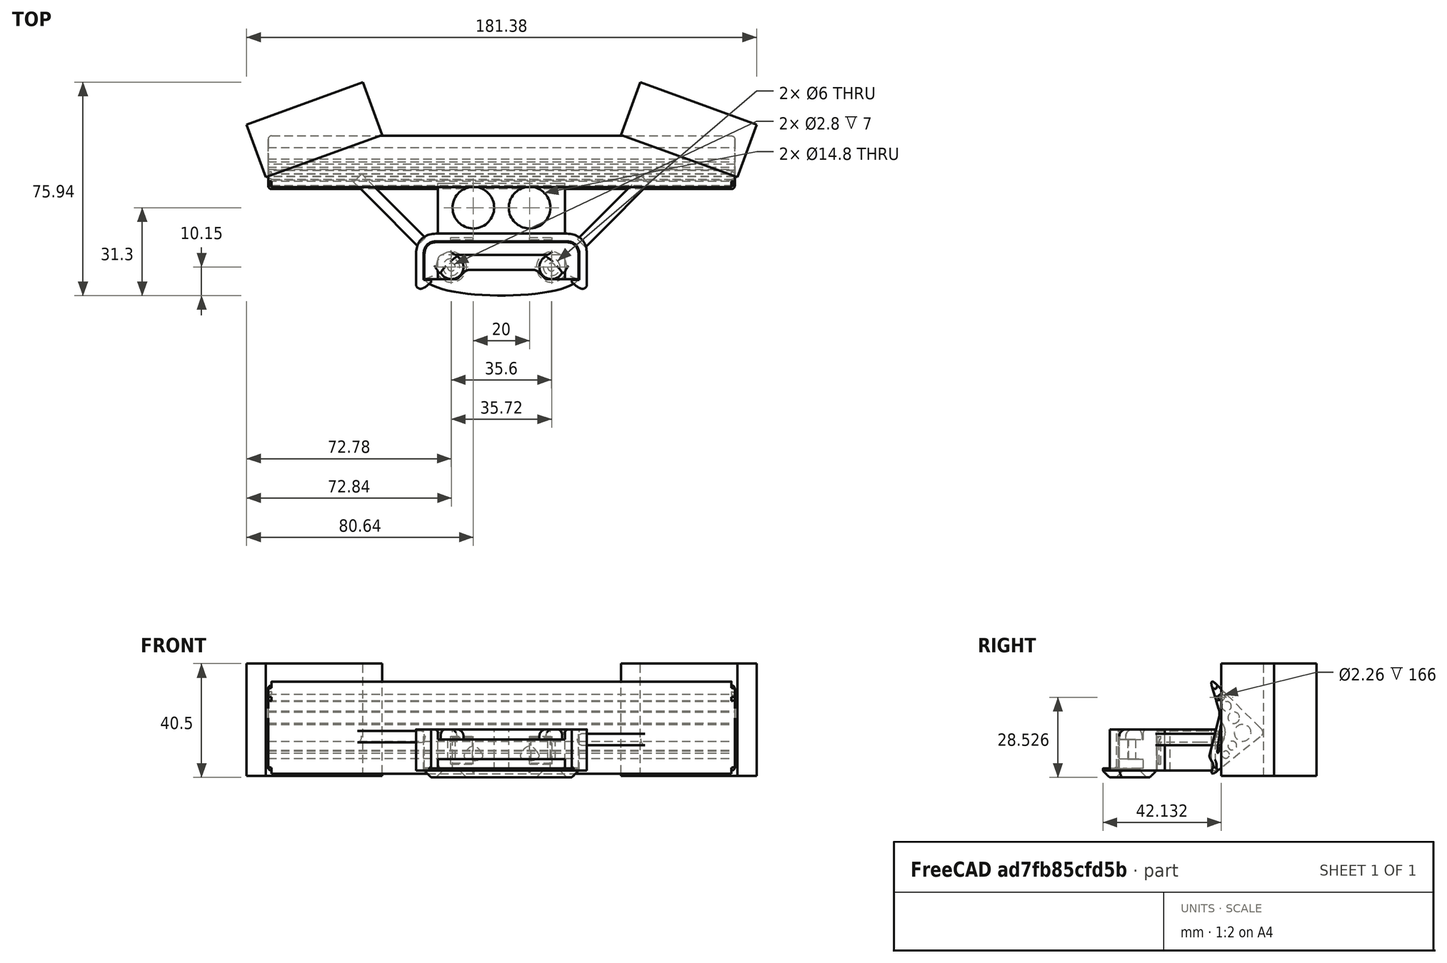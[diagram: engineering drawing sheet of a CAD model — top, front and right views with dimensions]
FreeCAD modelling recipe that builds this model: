
FCSTD DOCUMENT  (FreeCAD 0.21R0.20.1)
Label: 052
License: All rights reserved
LicenseURL: http://en.wikipedia.org/wiki/All_rights_reserved
objects: Part::Cylinder×8, Sketcher::SketchObject×7, Part::Extrusion×7, Part::Box×7, Part::MultiFuse×7, Part::Fillet×7, Part::Cut×4, Part::Chamfer×2
note: 49 computed .brp shape members not serialized (recipe doc carries the construction recipe); baked Part::Feature solids carry a one-line shape summary decoded from their .brp

FEATURE [Sketcher::SketchObject] Sketch  label="attatchmentPiece"
  FullyConstrained = true
  sketch-geometry (20):
    g0: LineSegment StartX=21.05 StartY=0 StartZ=0 EndX=21.05 EndY=-1 EndZ=0
    g1: LineSegment StartX=21.05 StartY=-1 StartZ=0 EndX=21.05 EndY=-4.3 EndZ=0
    g2: LineSegment StartX=-24.15 StartY=4.3 StartZ=0 EndX=21.05 EndY=4.3 EndZ=0
    g3: LineSegment StartX=21.05 StartY=0 StartZ=0 EndX=21.05 EndY=4.3 EndZ=0
    g4-g7: Circle x4 (B-spline internal-alignment scaffolding for g8; pole/knot coordinates omitted)
    g8: BSplineCurve PolesCount=4 KnotsCount=2 Degree=3 IsPeriodic=0
    g9: GeomPoint X=10.05 Y=-1 Z=0
    g10: GeomPoint X=14.55 Y=-4.3 Z=0
    g11: LineSegment StartX=10.05 StartY=-1 StartZ=0 EndX=-10.05 EndY=-1 EndZ=0
    g12: LineSegment StartX=14.55 StartY=-4.3 StartZ=0 EndX=21.05 EndY=-4.3 EndZ=0
    g13: LineSegment StartX=-24.15 StartY=4.3 StartZ=0 EndX=-24.15 EndY=-4.3 EndZ=0
    g14: LineSegment StartX=-13.15 StartY=-1 StartZ=0 EndX=-10.05 EndY=-1 EndZ=0
    g15: LineSegment StartX=-24.15 StartY=-4.3 StartZ=0 EndX=-19.35 EndY=-4.3 EndZ=0
    g16: LineSegment StartX=-19.35 StartY=-4.3 StartZ=0 EndX=-17.65 EndY=-4.3 EndZ=0
    g17: BSplineCurve PolesCount=4 KnotsCount=2 Degree=3 IsPeriodic=0
    g18: Circle CenterX=16.25 CenterY=0 CenterZ=0 NormalX=0 NormalY=0 NormalZ=1 AngleXU=0 Radius=1.4
    g19: Circle CenterX=-19.35 CenterY=0 CenterZ=0 NormalX=0 NormalY=0 NormalZ=1 AngleXU=0 Radius=1.4
  constraints (41):
    c: Vertical(g0)
    c: Coincident(g1,g0)
    c: Vertical(g1)
    c: Block(g0)
    c: Horizontal(g2)
    c: Vertical(g3)
    c: Coincident(g3,g2)
    c: Block(g2)
    c: Block(g3)
    c: Weight(g4) = 1
    c: Equal(g4,g5)
    c: Equal(g4,g6)
    c: Equal(g4,g7)
    c: InternalAlignment(g4-g7 -> g8) x4
    c: InternalAlignment(g9,g8)
    c: InternalAlignment(g10,g8)
    c: Block(g8)
    c: Coincident(g11,g8)
    c: Horizontal(g11)
    c: Coincident(g12,g8)
    c: Coincident(g12,g1)
    c: Horizontal(g12)
    c: Distance(g2) = 45.2
    c: Coincident(g13,g2)
    c: Vertical(g13)
    c: Horizontal(g14)
    c: Distance(g14) = 3.1
    c: Horizontal(g15)
    c: Block(g17)
    c: Coincident(g16,g15)
    c: Coincident(g16,g17)
    c: Horizontal(g16)
    c: Block(g16)
    c: Coincident(g17,g14)
    c: Block(g15)
    c: Block(g11)
    c: Block(g13)
    c: Distance(g15) = 4.8
    c: Distance(g16) = 1.7
    c: Block(g18)
    c: Block(g19)
FEATURE [Part::Extrusion] Extrude  label="attatchmentPiece001"
  Base = -> Sketch
  Dir = (0,0,1)
  DirMode = 2
  FaceMakerClass = Part::FaceMakerBullseye
  LengthFwd = 7
  LengthRev = 0
  Solid = true
  Symmetric = false
FEATURE [Sketcher::SketchObject] Sketch001  label="attatchmentPieceSurround"
  FullyConstrained = true
  sketch-geometry (18):
    g0: LineSegment StartX=25.85 StartY=-4.3 StartZ=0 EndX=21.05 EndY=-4.3 EndZ=0
    g1: LineSegment StartX=25.85 StartY=-4.3 StartZ=0 EndX=25.85 EndY=4.3 EndZ=0
    g2: LineSegment StartX=-21.05 StartY=8.9 StartZ=0 EndX=21.05 EndY=8.9 EndZ=0
    g3: Circle CenterX=21.05 CenterY=8.9 CenterZ=0 NormalX=0 NormalY=0 NormalZ=1 AngleXU=0 Radius=1
    g4: Circle CenterX=25.85 CenterY=8.9 CenterZ=0 NormalX=0 NormalY=0 NormalZ=1 AngleXU=0 Radius=1
    g5: Circle CenterX=25.85 CenterY=4.3 CenterZ=0 NormalX=0 NormalY=0 NormalZ=1 AngleXU=0 Radius=1
    g6: BSplineCurve PolesCount=3 KnotsCount=2 Degree=2 IsPeriodic=0
    g7: GeomPoint X=21.05 Y=8.9 Z=0
    g8: GeomPoint X=25.85 Y=4.3 Z=0
    g9: ArcOfCircle CenterX=19.45 CenterY=2.7 CenterZ=0 NormalX=0 NormalY=0 NormalZ=1 AngleXU=0 Radius=1.6 StartAngle=0 EndAngle=1.5708
    g10: LineSegment StartX=21.05 StartY=2.7 StartZ=0 EndX=21.05 EndY=-4.3 EndZ=0
    g11: BSplineCurve PolesCount=3 KnotsCount=2 Degree=2 IsPeriodic=0
    g12: LineSegment StartX=-28.95 StartY=-4.3 StartZ=0 EndX=-28.95 EndY=4.3 EndZ=0
    g13: LineSegment StartX=-24.15 StartY=-4.3 StartZ=0 EndX=-28.95 EndY=-4.3 EndZ=0
    g14: LineSegment StartX=-24.15 StartY=2.7 StartZ=0 EndX=-24.15 EndY=-4.3 EndZ=0
    g15: ArcOfCircle CenterX=-22.55 CenterY=2.7 CenterZ=0 NormalX=0 NormalY=0 NormalZ=1 AngleXU=0 Radius=1.6 StartAngle=1.5708 EndAngle=3.14159
    g16: LineSegment StartX=-24.15 StartY=8.9 StartZ=0 EndX=-21.05 EndY=8.9 EndZ=0
    g17: LineSegment StartX=-22.55 StartY=4.3 StartZ=0 EndX=19.45 EndY=4.3 EndZ=0
  constraints (38):
    c: Horizontal(g0)
    c: Vertical(g1)
    c: Coincident(g1,g0)
    c: Horizontal(g2)
    c: Distance(g2) = 42.1
    c: Block(g2)
    c: Coincident(g6,g2)
    c: Weight(g3) = 1
    c: Equal(g3,g4)
    c: Equal(g3,g5)
    c: Coincident(g6,g1)
    c: InternalAlignment(g3,g6)
    c: InternalAlignment(g4,g6)
    c: InternalAlignment(g5,g6)
    c: InternalAlignment(g7,g6)
    c: InternalAlignment(g8,g6)
    c: Block(g0)
    c: Block(g6)
    c: Block(g9)
    c: Coincident(g10,g9)
    c: Coincident(g10,g0)
    c: Vertical(g10)
    c: Horizontal(g13)
    c: Coincident(g12,g13)
    c: Vertical(g12)
    c: Coincident(g11,g12)
    c: Block(g12)
    c: Block(g11)
    c: Block(g15)
    c: Coincident(g14,g15)
    c: Coincident(g14,g13)
    c: Vertical(g14)
    c: Coincident(g16,g11)
    c: Coincident(g16,g2)
    c: Horizontal(g16)
    c: Coincident(g17,g15)
    c: Coincident(g17,g9)
    c: Horizontal(g17)
FEATURE [Part::Extrusion] Extrude001  label="attatchmentPieceSurround001"
  Base = -> Sketch001
  Dir = (0,0,1)
  DirMode = 2
  FaceMakerClass = Part::FaceMakerBullseye
  LengthFwd = 14.7
  LengthRev = 0
  Placement = pos=(0,0,-4.1) rot=(0,0,1;0rad)
  Solid = true
  Symmetric = false
FEATURE [Sketcher::SketchObject] Sketch002  label="attatchmentPieceEndScrewHoleCaps"
  FullyConstrained = true
  sketch-geometry (10):
    g0: ArcOfCircle CenterX=16.25 CenterY=0 CenterZ=0 NormalX=0 NormalY=0 NormalZ=1 AngleXU=0 Radius=4.3 StartAngle=2.05456 EndAngle=5.79942
    g1: LineSegment StartX=14.25 StartY=3.80657 StartZ=0 EndX=14.25 EndY=6 EndZ=0
    g2: LineSegment StartX=20.0566 StartY=-2 StartZ=0 EndX=22.25 EndY=-2 EndZ=0
    g3: LineSegment StartX=22.25 StartY=-2 StartZ=0 EndX=22.25 EndY=6 EndZ=0
    g4: LineSegment StartX=14.25 StartY=6 StartZ=0 EndX=22.25 EndY=6 EndZ=0
    g5: LineSegment StartX=-25.35 StartY=-2 StartZ=0 EndX=-25.35 EndY=6 EndZ=0
    g6: LineSegment StartX=-25.35 StartY=-2 StartZ=0 EndX=-23.1566 EndY=-2 EndZ=0
    g7: LineSegment StartX=-17.35 StartY=6 StartZ=0 EndX=-25.35 EndY=6 EndZ=0
    g8: LineSegment StartX=-17.35 StartY=3.80657 StartZ=0 EndX=-17.35 EndY=6 EndZ=0
    g9: ArcOfCircle CenterX=-19.35 CenterY=0 CenterZ=0 NormalX=0 NormalY=0 NormalZ=1 AngleXU=0 Radius=4.3 StartAngle=3.62536 EndAngle=7.37022
  constraints (25):
    c: Block(g0)
    c: Vertical(g1)
    c: Horizontal(g2)
    c: Coincident(g3,g2)
    c: Vertical(g3)
    c: Coincident(g4,g1)
    c: Horizontal(g4)
    c: Coincident(g3,g4)
    c: Block(g4)
    c: Block(g3)
    c: Coincident(g0,g1)
    c: Coincident(g0,g2)
    c: Block(g1)
    c: Block(g9)
    c: Horizontal(g6)
    c: Vertical(g8)
    c: Coincident(g7,g8)
    c: Horizontal(g7)
    c: Coincident(g5,g6)
    c: Vertical(g5)
    c: Coincident(g5,g7)
    c: Block(g7)
    c: Block(g5)
    c: Coincident(g9,g6)
    c: Coincident(g9,g8)
FEATURE [Part::Extrusion] Extrude002  label="attatchmentPieceEndScrewHoleCaps001"
  Base = -> Sketch002
  Dir = (0,0,1)
  DirMode = 2
  FaceMakerClass = Part::FaceMakerBullseye
  LengthFwd = 3.6
  LengthRev = 0
  Placement = pos=(0,0,7) rot=(0,0,1;0rad)
  Solid = true
  Symmetric = false
FEATURE [Sketcher::SketchObject] Sketch003  label="mainBumpperPieceAttatchment"
  FullyConstrained = true
  sketch-geometry (42):
    g0: Circle CenterX=28.85 CenterY=4.3 CenterZ=0 NormalX=0 NormalY=0 NormalZ=1 AngleXU=0 Radius=1
    g1: Circle CenterX=28.85 CenterY=11.9 CenterZ=0 NormalX=0 NormalY=0 NormalZ=1 AngleXU=0 Radius=1
    g2: Circle CenterX=21.05 CenterY=11.9 CenterZ=0 NormalX=0 NormalY=0 NormalZ=1 AngleXU=0 Radius=1
    g3: BSplineCurve PolesCount=3 KnotsCount=2 Degree=2 IsPeriodic=0
    g4: GeomPoint X=28.85 Y=4.3 Z=0
    g5: GeomPoint X=21.05 Y=11.9 Z=0
    g6: LineSegment StartX=-21.05 StartY=11.9 StartZ=0 EndX=21.05 EndY=11.9 EndZ=0
    g7: LineSegment StartX=28.85 StartY=4.3 StartZ=0 EndX=28.85 EndY=-4.3 EndZ=0
    g8: Circle CenterX=21.05 CenterY=9.2 CenterZ=0 NormalX=0 NormalY=0 NormalZ=1 AngleXU=0 Radius=1
    g9: Circle CenterX=26.15 CenterY=9.2 CenterZ=0 NormalX=0 NormalY=0 NormalZ=1 AngleXU=0 Radius=1
    g10: Circle CenterX=26.15 CenterY=4.3 CenterZ=0 NormalX=0 NormalY=0 NormalZ=1 AngleXU=0 Radius=1
    g11: BSplineCurve PolesCount=3 KnotsCount=2 Degree=2 IsPeriodic=0
    g12: GeomPoint X=21.05 Y=9.2 Z=0
    g13: GeomPoint X=26.15 Y=4.3 Z=0
    g14: LineSegment StartX=-21.05 StartY=9.2 StartZ=0 EndX=21.05 EndY=9.2 EndZ=0
    g15: LineSegment StartX=26.15 StartY=-4.3 StartZ=0 EndX=26.15 EndY=4.3 EndZ=0
    g16: LineSegment StartX=26.15 StartY=-4.3 StartZ=0 EndX=26.15 EndY=-4.6 EndZ=0
    g17: LineSegment StartX=23.45 StartY=-4.6 StartZ=0 EndX=26.15 EndY=-4.6 EndZ=0
    g18: LineSegment StartX=28.85 StartY=-4.3 StartZ=0 EndX=28.85 EndY=-7.9 EndZ=0
    g19: LineSegment StartX=23.45 StartY=-4.6 StartZ=0 EndX=23.45 EndY=-5.3 EndZ=0
    g20: Circle CenterX=28.85 CenterY=-7.9 CenterZ=0 NormalX=0 NormalY=0 NormalZ=1 AngleXU=0 Radius=1
    g21: Circle CenterX=26.15 CenterY=-8.2 CenterZ=0 NormalX=0 NormalY=0 NormalZ=1 AngleXU=0 Radius=1
    g22: Circle CenterX=23.45 CenterY=-5.3 CenterZ=0 NormalX=0 NormalY=0 NormalZ=1 AngleXU=0 Radius=1
    g23: BSplineCurve PolesCount=3 KnotsCount=2 Degree=2 IsPeriodic=0
    g24: GeomPoint X=28.85 Y=-7.9 Z=0
    g25: GeomPoint X=23.45 Y=-5.3 Z=0
    g26: LineSegment StartX=-21.05 StartY=9.2 StartZ=0 EndX=-24.15 EndY=9.2 EndZ=0
    g27: BSplineCurve PolesCount=3 KnotsCount=2 Degree=2 IsPeriodic=0
    g28: LineSegment StartX=-29.25 StartY=-4.3 StartZ=0 EndX=-29.25 EndY=-4.6 EndZ=0
    g29: LineSegment StartX=-29.25 StartY=-4.6 StartZ=0 EndX=-26.55 EndY=-4.6 EndZ=0
    g30: LineSegment StartX=-31.95 StartY=-4.3 StartZ=0 EndX=-31.95 EndY=-7.9 EndZ=0
    g31: LineSegment StartX=-26.55 StartY=-4.6 StartZ=0 EndX=-26.55 EndY=-5.3 EndZ=0
    g32: Circle CenterX=-31.95 CenterY=-7.9 CenterZ=0 NormalX=0 NormalY=0 NormalZ=1 AngleXU=0 Radius=1
    g33: Circle CenterX=-29.25 CenterY=-8.2 CenterZ=0 NormalX=0 NormalY=0 NormalZ=1 AngleXU=0 Radius=1
    g34: Circle CenterX=-26.55 CenterY=-5.3 CenterZ=0 NormalX=0 NormalY=0 NormalZ=1 AngleXU=0 Radius=1
    g35: BSplineCurve PolesCount=3 KnotsCount=2 Degree=2 IsPeriodic=0
    g36: GeomPoint X=-31.95 Y=-7.9 Z=0
    g37: GeomPoint X=-26.55 Y=-5.3 Z=0
    g38: LineSegment StartX=-31.95 StartY=4.3 StartZ=0 EndX=-31.95 EndY=-4.3 EndZ=0
    g39: LineSegment StartX=-29.25 StartY=-4.3 StartZ=0 EndX=-29.25 EndY=4.3 EndZ=0
    g40: BSplineCurve PolesCount=3 KnotsCount=2 Degree=2 IsPeriodic=0
    g41: LineSegment StartX=-21.05 StartY=11.9 StartZ=0 EndX=-24.15 EndY=11.9 EndZ=0
  constraints (78):
    c: Weight(g0) = 1
    c: Equal(g0,g1)
    c: Equal(g0,g2)
    c: InternalAlignment(g0,g3)
    c: InternalAlignment(g1,g3)
    c: InternalAlignment(g2,g3)
    c: InternalAlignment(g4,g3)
    c: InternalAlignment(g5,g3)
    c: Block(g3)
    c: Horizontal(g6)
    c: Vertical(g7)
    c: Block(g7)
    c: Block(g6)
    c: Weight(g8) = 1
    c: Equal(g8,g9)
    c: Equal(g8,g10)
    c: InternalAlignment(g8,g11)
    c: InternalAlignment(g9,g11)
    c: InternalAlignment(g10,g11)
    c: InternalAlignment(g12,g11)
    c: InternalAlignment(g13,g11)
    c: Horizontal(g14)
    c: Vertical(g15)
    c: Block(g11)
    c: Block(g15)
    c: Block(g14)
    c: Coincident(g16,g15)
    c: Vertical(g16)
    c: Distance(g16) = 0.3
    c: Horizontal(g17)
    c: Coincident(g17,g16)
    c: Coincident(g18,g7)
    c: Vertical(g18)
    c: Distance(g18) = 3.6
    c: Vertical(g19)
    c: Coincident(g19,g17)
    c: Coincident(g23,g18)
    c: Weight(g20) = 1
    c: Equal(g20,g21)
    c: Equal(g20,g22)
    c: Coincident(g23,g19)
    c: InternalAlignment(g20,g23)
    c: InternalAlignment(g21,g23)
    c: InternalAlignment(g22,g23)
    c: InternalAlignment(g24,g23)
    c: InternalAlignment(g25,g23)
    c: Block(g23)
    c: Horizontal(g26)
    c: Distance(g26) = 3.1
    c: Block(g27)
    c: Vertical(g38)
    c: Block(g38)
    c: Vertical(g39)
    c: Block(g40)
    c: Block(g39)
    c: Vertical(g28)
    c: Coincident(g28,g39)
    c: Coincident(g29,g28)
    c: Horizontal(g29)
    c: Vertical(g30)
    c: Coincident(g30,g38)
    c: Coincident(g31,g29)
    c: Vertical(g31)
    c: Coincident(g35,g30)
    c: Equal(g32,g33)
    c: Equal(g32,g34)
    c: Coincident(g35,g31)
    c: InternalAlignment(g32,g35)
    c: InternalAlignment(g33,g35)
    c: InternalAlignment(g34,g35)
    c: InternalAlignment(g36,g35)
    c: InternalAlignment(g37,g35)
    c: Block(g35)
    c: Coincident(g40,g26)
    c: Block(g29)
    c: Horizontal(g41)
    c: Equal(g26,g41) = 3.1
    c: Coincident(g41,g6)
FEATURE [Part::Box] Box  label="bumpperExtension"
  AttacherType = Attacher::AttachEngine3D
  Height = 14.7
  Length = 45.2
  Placement = pos=(-24.15,11.9,-4.1) rot=(0,0,1;0rad)
  Width = 18
FEATURE [Sketcher::SketchObject] Sketch004  label="bumpperMain"
  FullyConstrained = true
  Placement = pos=(0,0,0) rot=(0.57735,0.57735,0.57735;2.0944rad)
  sketch-geometry (62):
    g0: Circle CenterX=-3.12329 CenterY=2.49901 CenterZ=0 NormalX=0 NormalY=0 NormalZ=1 AngleXU=0 Radius=1
    g1: Circle CenterX=0 CenterY=0 CenterZ=0 NormalX=0 NormalY=0 NormalZ=1 AngleXU=0 Radius=1
    g2: Circle CenterX=-1.35243 CenterY=3.60648 CenterZ=0 NormalX=0 NormalY=0 NormalZ=1 AngleXU=0 Radius=1
    g3: BSplineCurve PolesCount=3 KnotsCount=2 Degree=2 IsPeriodic=0
    g4: GeomPoint X=-3.12329 Y=2.49901 Z=0
    g5: GeomPoint X=-1.35243 Y=3.60648 Z=0
    g6: Circle CenterX=-2.83953 CenterY=33.0261 CenterZ=0 NormalX=0 NormalY=0 NormalZ=1 AngleXU=0 Radius=1
    g7: Circle CenterX=0 CenterY=35.8434 CenterZ=0 NormalX=0 NormalY=0 NormalZ=1 AngleXU=0 Radius=1
    g8: Circle CenterX=-1.15771 CenterY=32.0146 CenterZ=0 NormalX=0 NormalY=0 NormalZ=1 AngleXU=0 Radius=1
    g9: BSplineCurve PolesCount=3 KnotsCount=2 Degree=2 IsPeriodic=0
    g10: GeomPoint X=-2.83953 Y=33.0261 Z=0
    g11: GeomPoint X=-1.15771 Y=32.0146 Z=0
    g12: Circle CenterX=-18.2963 CenterY=17.6904 CenterZ=0 NormalX=0 NormalY=0 NormalZ=1 AngleXU=0 Radius=1
    g13: Circle CenterX=-20 CenterY=16 CenterZ=0 NormalX=0 NormalY=0 NormalZ=1 AngleXU=0 Radius=1
    g14: Circle CenterX=-18.1259 CenterY=14.5008 CenterZ=0 NormalX=0 NormalY=0 NormalZ=1 AngleXU=0 Radius=1
    g15: BSplineCurve PolesCount=3 KnotsCount=2 Degree=2 IsPeriodic=0
    g16: GeomPoint X=-18.2963 Y=17.6904 Z=0
    g17: GeomPoint X=-18.1259 Y=14.5008 Z=0
    g18: LineSegment StartX=-18.2963 StartY=17.6904 StartZ=0 EndX=-2.83953 EndY=33.0261 EndZ=0
    g19: LineSegment StartX=-18.1259 StartY=14.5008 StartZ=0 EndX=-3.12329 EndY=2.49901 EndZ=0
    g20: Circle CenterX=-11.9527 CenterY=16 CenterZ=0 NormalX=0 NormalY=0 NormalZ=1 AngleXU=0 Radius=2.99582
    g21: Circle CenterX=-8.803 CenterY=21.3731 CenterZ=0 NormalX=0 NormalY=0 NormalZ=1 AngleXU=0 Radius=2.03939
    g22: Circle CenterX=-6.23123 CenterY=25.4475 CenterZ=0 NormalX=0 NormalY=0 NormalZ=1 AngleXU=0 Radius=1.69309
    g23: Circle CenterX=-4.38186 CenterY=28.6261 CenterZ=0 NormalX=0 NormalY=0 NormalZ=1 AngleXU=0 Radius=1.13029
    g24: Circle CenterX=-8.28033 CenterY=11.4296 CenterZ=0 NormalX=0 NormalY=0 NormalZ=1 AngleXU=0 Radius=1.57213
    g25: Circle CenterX=-5.93972 CenterY=8.22213 CenterZ=0 NormalX=0 NormalY=0 NormalZ=1 AngleXU=0 Radius=1.28743
    g26: Circle CenterX=-3.47023 CenterY=24.3665 CenterZ=0 NormalX=0 NormalY=0 NormalZ=1 AngleXU=0 Radius=1
    g27: Circle CenterX=-3.90437 CenterY=22.9307 CenterZ=0 NormalX=0 NormalY=0 NormalZ=1 AngleXU=0 Radius=1
    g28: Circle CenterX=-3.53772 CenterY=21.4762 CenterZ=0 NormalX=0 NormalY=0 NormalZ=1 AngleXU=0 Radius=1
    g29: BSplineCurve PolesCount=3 KnotsCount=2 Degree=2 IsPeriodic=0
    g30: GeomPoint X=-3.47023 Y=24.3665 Z=0
    g31: GeomPoint X=-3.53772 Y=21.4762 Z=0
    g32: LineSegment StartX=-1.15771 StartY=32.0146 StartZ=0 EndX=-3.47023 EndY=24.3665 EndZ=0
    g33: Circle CenterX=-5.41867 CenterY=17.9226 CenterZ=0 NormalX=0 NormalY=0 NormalZ=1 AngleXU=0 Radius=1
    g34: Circle CenterX=-6 CenterY=16 CenterZ=0 NormalX=0 NormalY=0 NormalZ=1 AngleXU=0 Radius=1
    g35: Circle CenterX=-5.22753 CenterY=13.9401 CenterZ=0 NormalX=0 NormalY=0 NormalZ=1 AngleXU=0 Radius=1
    g36: BSplineCurve PolesCount=3 KnotsCount=2 Degree=2 IsPeriodic=0
    g37: GeomPoint X=-5.41867 Y=17.9226 Z=0
    g38: GeomPoint X=-5.22753 Y=13.9401 Z=0
    g39: Circle CenterX=-3.98946 CenterY=10.6386 CenterZ=0 NormalX=0 NormalY=0 NormalZ=1 AngleXU=0 Radius=1
    g40: Circle CenterX=-2.58497 CenterY=6.89324 CenterZ=0 NormalX=0 NormalY=0 NormalZ=1 AngleXU=0 Radius=1
    g41: Circle CenterX=-3.11001 CenterY=10.8586 CenterZ=0 NormalX=0 NormalY=0 NormalZ=1 AngleXU=0 Radius=1
    g42: BSplineCurve PolesCount=3 KnotsCount=2 Degree=2 IsPeriodic=0
    g43: GeomPoint X=-3.98946 Y=10.6386 Z=0
    g44: GeomPoint X=-3.11001 Y=10.8586 Z=0
    g45: Circle CenterX=-1.35243 CenterY=3.60648 CenterZ=0 NormalX=0 NormalY=0 NormalZ=1 AngleXU=0 Radius=1
    g46: Circle CenterX=-1.76142 CenterY=4.69712 CenterZ=0 NormalX=0 NormalY=0 NormalZ=1 AngleXU=0 Radius=1
    g47: Circle CenterX=-1.05937 CenterY=5.79125 CenterZ=0 NormalX=0 NormalY=0 NormalZ=1 AngleXU=0 Radius=1
    g48: BSplineCurve PolesCount=3 KnotsCount=2 Degree=2 IsPeriodic=0
    g49: GeomPoint X=-1.35243 Y=3.60648 Z=0
    g50: GeomPoint X=-1.05937 Y=5.79125 Z=0
    g51: Circle CenterX=-0.519336 CenterY=6.6329 CenterZ=0 NormalX=0 NormalY=0 NormalZ=1 AngleXU=0 Radius=1
    g52: Circle CenterX=0 CenterY=7.44228 CenterZ=0 NormalX=0 NormalY=0 NormalZ=1 AngleXU=0 Radius=1
    g53: Circle CenterX=-0.244436 CenterY=8.41194 CenterZ=0 NormalX=0 NormalY=0 NormalZ=1 AngleXU=0 Radius=1
    g54: BSplineCurve PolesCount=3 KnotsCount=2 Degree=2 IsPeriodic=0
    g55: GeomPoint X=-0.519336 Y=6.6329 Z=0
    g56: GeomPoint X=-0.244436 Y=8.41194 Z=0
    g57: LineSegment StartX=-3.53772 StartY=21.4762 StartZ=0 EndX=-0.244436 EndY=8.41194 EndZ=0
    g58: LineSegment StartX=-5.22753 StartY=13.9401 StartZ=0 EndX=-3.98946 EndY=10.6386 EndZ=0
    g59: LineSegment StartX=-1.05937 StartY=5.79125 StartZ=0 EndX=-0.519336 EndY=6.6329 EndZ=0
    g60: BSplineCurve PolesCount=3 KnotsCount=2 Degree=2 IsPeriodic=0
    g61: LineSegment StartX=-4.0304 StartY=17.8099 StartZ=0 EndX=-3.11001 EndY=10.8586 EndZ=0
  constraints (96):
    c: Weight(g0) = 1
    c: Equal(g0,g1)
    c: Equal(g0,g2)
    c: InternalAlignment(g0,g3)
    c: InternalAlignment(g1,g3)
    c: InternalAlignment(g2,g3)
    c: InternalAlignment(g4,g3)
    c: InternalAlignment(g5,g3)
    c: Block(g3)
    c: Weight(g6) = 1
    c: Equal(g6,g7)
    c: Equal(g6,g8)
    c: InternalAlignment(g6,g9)
    c: InternalAlignment(g7,g9)
    c: InternalAlignment(g8,g9)
    c: InternalAlignment(g10,g9)
    c: InternalAlignment(g11,g9)
    c: Block(g9)
    c: Weight(g12) = 1
    c: Equal(g12,g13)
    c: Equal(g12,g14)
    c: InternalAlignment(g12,g15)
    c: InternalAlignment(g13,g15)
    c: InternalAlignment(g14,g15)
    c: InternalAlignment(g16,g15)
    c: InternalAlignment(g17,g15)
    c: Block(g15)
    c: Coincident(g18,g15)
    c: Coincident(g18,g9)
    c: Coincident(g19,g15)
    c: Coincident(g19,g3)
    c: Block(g25)
    c: Block(g24)
    c: Block(g20)
    c: Block(g21)
    c: Block(g22)
    c: Block(g23)
    c: Weight(g26) = 1
    c: Equal(g26,g27)
    c: Equal(g26,g28)
    c: InternalAlignment(g26,g29)
    c: InternalAlignment(g27,g29)
    c: InternalAlignment(g28,g29)
    c: InternalAlignment(g30,g29)
    c: InternalAlignment(g31,g29)
    c: Block(g29)
    c: Coincident(g32,g9)
    c: Coincident(g32,g29)
    c: Weight(g33) = 1
    c: Equal(g33,g34)
    c: Equal(g33,g35)
    c: InternalAlignment(g33,g36)
    c: InternalAlignment(g34,g36)
    c: InternalAlignment(g35,g36)
    c: InternalAlignment(g37,g36)
    c: InternalAlignment(g38,g36)
    c: Block(g36)
    c: Weight(g39) = 1
    c: Equal(g39,g40)
    c: Equal(g39,g41)
    c: InternalAlignment(g39,g42)
    c: InternalAlignment(g40,g42)
    c: InternalAlignment(g41,g42)
    c: InternalAlignment(g43,g42)
    c: InternalAlignment(g44,g42)
    c: Block(g42)
    c: Coincident(g48,g3)
    c: Weight(g45) = 1
    c: Equal(g45,g46)
    c: Equal(g45,g47)
    c: InternalAlignment(g45,g48)
    c: InternalAlignment(g46,g48)
    c: InternalAlignment(g47,g48)
    c: InternalAlignment(g49,g48)
    c: InternalAlignment(g50,g48)
    c: Block(g48)
    c: Weight(g51) = 1
    c: Equal(g51,g52)
    c: Equal(g51,g53)
    c: InternalAlignment(g51,g54)
    c: InternalAlignment(g52,g54)
    c: InternalAlignment(g53,g54)
    c: InternalAlignment(g55,g54)
    c: InternalAlignment(g56,g54)
    c: Block(g54)
    c: Coincident(g57,g29)
    c: Coincident(g57,g54)
    c: Block(g57)
    c: Coincident(g58,g36)
    c: Coincident(g58,g42)
    c: Coincident(g59,g48)
    c: Coincident(g59,g54)
    c: Block(g60)
    c: Coincident(g60,g36)
    c: Coincident(g61,g60)
    c: Coincident(g61,g42)
FEATURE [Part::Extrusion] Extrude004  label="bumpperMain001"
  Base = -> Sketch004
  Dir = (1,0,0)
  DirMode = 2
  FaceMakerClass = Part::FaceMakerBullseye
  LengthFwd = 166
  LengthRev = 0
  Placement = pos=(81.45,27.6,-6.6) rot=(0,0,1;3.14159rad)
  Solid = true
  Symmetric = false
FEATURE [Sketcher::SketchObject] Sketch005  label="attatchmentPieceBottom"
  FullyConstrained = true
  sketch-geometry (20):
    g0: LineSegment StartX=25.85 StartY=-4.3 StartZ=0 EndX=25.85 EndY=4.3 EndZ=0
    g1: LineSegment StartX=-21.05 StartY=8.9 StartZ=0 EndX=21.05 EndY=8.9 EndZ=0
    g2: Circle CenterX=21.05 CenterY=8.9 CenterZ=0 NormalX=0 NormalY=0 NormalZ=1 AngleXU=0 Radius=1
    g3: Circle CenterX=25.85 CenterY=8.9 CenterZ=0 NormalX=0 NormalY=0 NormalZ=1 AngleXU=0 Radius=1
    g4: Circle CenterX=25.85 CenterY=4.3 CenterZ=0 NormalX=0 NormalY=0 NormalZ=1 AngleXU=0 Radius=1
    g5: BSplineCurve PolesCount=3 KnotsCount=2 Degree=2 IsPeriodic=0
    g6: GeomPoint X=21.05 Y=8.9 Z=0
    g7: GeomPoint X=25.85 Y=4.3 Z=0
    g8: BSplineCurve PolesCount=3 KnotsCount=2 Degree=2 IsPeriodic=0
    g9: LineSegment StartX=-28.95 StartY=-4.3 StartZ=0 EndX=-28.95 EndY=4.3 EndZ=0
    g10: LineSegment StartX=-24.15 StartY=8.9 StartZ=0 EndX=-21.05 EndY=8.9 EndZ=0
    g11: Circle CenterX=-19.41 CenterY=0 CenterZ=0 NormalX=0 NormalY=0 NormalZ=1 AngleXU=0 Radius=3
    g12: Circle CenterX=16.3103 CenterY=0 CenterZ=0 NormalX=0 NormalY=0 NormalZ=1 AngleXU=0 Radius=3
    g13-g16: Circle x4 (B-spline internal-alignment scaffolding for g17; pole/knot coordinates omitted)
    g17: BSplineCurve PolesCount=4 KnotsCount=2 Degree=3 IsPeriodic=0
    g18: GeomPoint X=-28.95 Y=-4.3 Z=0
    g19: GeomPoint X=25.85 Y=-4.3 Z=0
  constraints (36):
    c: Vertical(g0)
    c: Horizontal(g1)
    c: Distance(g1) = 42.1
    c: Block(g1)
    c: Coincident(g5,g1)
    c: Weight(g2) = 1
    c: Equal(g2,g3)
    c: Equal(g2,g4)
    c: Coincident(g5,g0)
    c: InternalAlignment(g2,g5)
    c: InternalAlignment(g3,g5)
    c: InternalAlignment(g4,g5)
    c: InternalAlignment(g6,g5)
    c: InternalAlignment(g7,g5)
    c: Block(g5)
    c: Vertical(g9)
    c: Coincident(g8,g9)
    c: Block(g9)
    c: Block(g8)
    c: Coincident(g10,g8)
    c: Coincident(g10,g1)
    c: Horizontal(g10)
    c: PointOnObject(g12,g-1)
    c: PointOnObject(g11,g-1)
    c: Block(g11)
    c: Block(g12)
    c: Coincident(g17,g9)
    c: Weight(g13) = 1
    c: Equal(g13,g14)
    c: Equal(g13,g15)
    c: Equal(g13,g16)
    c: Coincident(g17,g0)
    c: InternalAlignment(g13-g16 -> g17) x4
    c: InternalAlignment(g18,g17)
    c: InternalAlignment(g19,g17)
    c: Block(g17)
FEATURE [Part::Extrusion] Extrude005  label="removeFromMainBumpperPieceAttatchment"
  Base = -> Sketch005
  Dir = (0,0,1)
  DirMode = 2
  FaceMakerClass = Part::FaceMakerBullseye
  LengthFwd = 3.2
  LengthRev = 0
  Placement = pos=(0,0,-6.2) rot=(0,0,1;0rad)
  Solid = true
  Symmetric = false
FEATURE [Part::Extrusion] Extrude006  label="mainBumpperPieceAttatchment001"
  Base = -> Sketch003
  Dir = (0,0,1)
  DirMode = 2
  FaceMakerClass = Part::FaceMakerBullseye
  LengthFwd = 14.7
  LengthRev = 0
  Placement = pos=(0,0,-4.1) rot=(0,0,1;0rad)
  Solid = true
  Symmetric = false
FEATURE [Part::Cylinder] Cylinder  label="removeFromBumpperExtension"
  Angle = 360
  AttacherType = Attacher::AttachEngine3D
  FirstAngle = 0
  Height = 20
  Placement = pos=(8.45,21.15,-8) rot=(0,0,1;0rad)
  Radius = 7.4
  SecondAngle = 0
FEATURE [Part::Cylinder] Cylinder001  label="removeFromBumpperExtension001"
  Angle = 360
  AttacherType = Attacher::AttachEngine3D
  FirstAngle = 0
  Height = 20
  Placement = pos=(-11.55,21.15,-8) rot=(0,0,1;0rad)
  Radius = 7.4
  SecondAngle = 0
FEATURE [Part::MultiFuse] Fusion  label="removeFromBumpperExtension002"
  Shapes = -> [Cylinder,Cylinder001]
FEATURE [Part::Cylinder] Cylinder002  label="removeFromBumpperExtension004"
  Angle = 360
  AttacherType = Attacher::AttachEngine3D
  FirstAngle = 0
  Height = 20
  Placement = pos=(8.45,21.15,-8) rot=(0,0,1;0rad)
  Radius = 7.4
  SecondAngle = 0
FEATURE [Part::Cylinder] Cylinder003  label="removeFromBumpperExtension005"
  Angle = 360
  AttacherType = Attacher::AttachEngine3D
  FirstAngle = 0
  Height = 20
  Placement = pos=(-11.55,21.15,-8) rot=(0,0,1;0rad)
  Radius = 7.4
  SecondAngle = 0
FEATURE [Part::MultiFuse] Fusion001  label="removeFromBumpperMain"
  Shapes = -> [Cylinder002,Cylinder003]
FEATURE [Part::Cut] Cut  label="bumpperExtension001"
  Base = -> Box
  Tool = -> Fusion
FEATURE [Part::Fillet] Fillet  label="bumpperExtension002"
  Base = -> Cut
  Edges = 4 edges r=3: [Edge2,Edge4,Edge9,Edge14]
FEATURE [Part::Box] Box001  label="bumpperExtensionBumpHole"
  AttacherType = Attacher::AttachEngine3D
  Height = 10
  Length = 8
  Placement = pos=(8.45,9.2,-1.8) rot=(0,0,1;0rad)
  Width = 1.3
FEATURE [Part::Box] Box002  label="bumpperExtensionBumpHole001"
  AttacherType = Attacher::AttachEngine3D
  Height = 10
  Length = 8
  Placement = pos=(-19.55,9.2,-1.8) rot=(0,0,1;0rad)
  Width = 1.3
FEATURE [Part::Box] Box003  label="attatchmentPieceSurroundBump"
  AttacherType = Attacher::AttachEngine3D
  Height = 9.2
  Length = 7.2
  Placement = pos=(8.85,8.9,-1.4) rot=(0,0,1;0rad)
  Width = 1.3
FEATURE [Part::Box] Box004  label="attatchmentPieceSurroundBump001"
  AttacherType = Attacher::AttachEngine3D
  Height = 9.2
  Length = 7.2
  Placement = pos=(-19.15,8.9,-1.4) rot=(0,0,1;0rad)
  Width = 1.3
FEATURE [Part::MultiFuse] Fusion002  label="attatchmentPieceSurroundBump002"
  Placement = pos=(0,-0.4,0) rot=(0,0,1;0rad)
  Shapes = -> [Box004,Box003]
FEATURE [Part::MultiFuse] Fusion003  label="bumpperExtensionBumpHole002"
  Shapes = -> [Box002,Box001]
FEATURE [Part::Cut] Cut002  label="mainBumpperPieceAttatchment002"
  Base = -> Extrude006
  Tool = -> Fusion003
FEATURE [Part::Fillet] Fillet003  label="attatchmentPieceEndScrewHoleCaps002"
  Base = -> Extrude002
  Edges = 6 edges r=2.4: [Edge4,Edge7,Edge15,Edge25,Edge28,Edge30]
FEATURE [Part::Fillet] Fillet004  label="attatchmentPieceSurround002"
  Base = -> Extrude001
  Edges = 3 edges r=1.2: [Edge19,Edge25,Edge31]
FEATURE [Part::Fillet] Fillet006  label="mainBumpperPieceAttatchment003"
  Base = -> Cut002
  Edges = 2 edges r=1.6: [Edge2,Edge55]
FEATURE [Sketcher::SketchObject] Sketch006  label="attatchmentPieceBottom002"
  FullyConstrained = true
  sketch-geometry (20):
    g0: LineSegment StartX=25.85 StartY=-4.3 StartZ=0 EndX=25.85 EndY=4.3 EndZ=0
    g1: LineSegment StartX=-21.05 StartY=8.9 StartZ=0 EndX=21.05 EndY=8.9 EndZ=0
    g2: Circle CenterX=21.05 CenterY=8.9 CenterZ=0 NormalX=0 NormalY=0 NormalZ=1 AngleXU=0 Radius=1
    g3: Circle CenterX=25.85 CenterY=8.9 CenterZ=0 NormalX=0 NormalY=0 NormalZ=1 AngleXU=0 Radius=1
    g4: Circle CenterX=25.85 CenterY=4.3 CenterZ=0 NormalX=0 NormalY=0 NormalZ=1 AngleXU=0 Radius=1
    g5: BSplineCurve PolesCount=3 KnotsCount=2 Degree=2 IsPeriodic=0
    g6: GeomPoint X=21.05 Y=8.9 Z=0
    g7: GeomPoint X=25.85 Y=4.3 Z=0
    g8: BSplineCurve PolesCount=3 KnotsCount=2 Degree=2 IsPeriodic=0
    g9: LineSegment StartX=-28.95 StartY=-4.3 StartZ=0 EndX=-28.95 EndY=4.3 EndZ=0
    g10: LineSegment StartX=-24.15 StartY=8.9 StartZ=0 EndX=-21.05 EndY=8.9 EndZ=0
    g11: Circle CenterX=-19.41 CenterY=0 CenterZ=0 NormalX=0 NormalY=0 NormalZ=1 AngleXU=0 Radius=3
    g12: Circle CenterX=16.3103 CenterY=0 CenterZ=0 NormalX=0 NormalY=0 NormalZ=1 AngleXU=0 Radius=3
    g13-g16: Circle x4 (B-spline internal-alignment scaffolding for g17; pole/knot coordinates omitted)
    g17: BSplineCurve PolesCount=4 KnotsCount=2 Degree=3 IsPeriodic=0
    g18: GeomPoint X=-28.95 Y=-4.3 Z=0
    g19: GeomPoint X=25.85 Y=-4.3 Z=0
  constraints (36):
    c: Vertical(g0)
    c: Horizontal(g1)
    c: Distance(g1) = 42.1
    c: Block(g1)
    c: Coincident(g5,g1)
    c: Weight(g2) = 1
    c: Equal(g2,g3)
    c: Equal(g2,g4)
    c: Coincident(g5,g0)
    c: InternalAlignment(g2,g5)
    c: InternalAlignment(g3,g5)
    c: InternalAlignment(g4,g5)
    c: InternalAlignment(g6,g5)
    c: InternalAlignment(g7,g5)
    c: Block(g5)
    c: Vertical(g9)
    c: Coincident(g8,g9)
    c: Block(g9)
    c: Block(g8)
    c: Coincident(g10,g8)
    c: Coincident(g10,g1)
    c: Horizontal(g10)
    c: PointOnObject(g12,g-1)
    c: PointOnObject(g11,g-1)
    c: Block(g11)
    c: Block(g12)
    c: Coincident(g17,g9)
    c: Weight(g13) = 1
    c: Equal(g13,g14)
    c: Equal(g13,g15)
    c: Equal(g13,g16)
    c: Coincident(g17,g0)
    c: InternalAlignment(g13-g16 -> g17) x4
    c: InternalAlignment(g18,g17)
    c: InternalAlignment(g19,g17)
    c: Block(g17)
FEATURE [Part::Extrusion] Extrude007  label="attatchmentPieceBottom003"
  Base = -> Sketch006
  Dir = (0,0,1)
  DirMode = 2
  FaceMakerClass = Part::FaceMakerBullseye
  LengthFwd = 3.2
  LengthRev = 0
  Placement = pos=(0,0,-6.5) rot=(0,0,1;0rad)
  Solid = true
  Symmetric = false
FEATURE [Part::Cut] Cut003  label="mainBumpperPieceAttatchment004"
  Base = -> Fillet006
  Tool = -> Extrude005
FEATURE [Part::Chamfer] Chamfer
  Base = -> Extrude007
  Edges = 2 edges r=2.4: [Edge23,Edge26]
FEATURE [Part::Chamfer] Chamfer001  label="attatchmentPieceBottom004"
  Base = -> Chamfer
  Edges = 7 edges r=2.4: [Edge14,Edge15,Edge16,Edge17,Edge18,Edge19,Edge20]
FEATURE [Part::Fillet] Fillet007  label="attatchmentPieceBottom005"
  Base = -> Chamfer001
  Edges = 7 edges r=1.2: [Edge1,Edge2,Edge3,Edge4,Edge5,Edge6,Edge7]
FEATURE [Part::MultiFuse] Fusion007  label="attatchment"
  Shapes = -> [Fillet007,Fillet004,Fillet003,Fusion002,Extrude]
FEATURE [Part::Cut] Cut001  label="bumpperMain002"
  Base = -> Extrude004
  Tool = -> Fusion001
FEATURE [Part::Fillet] Fillet001
  Base = -> Cut001
  Edges = 11 edges r=1.2: [Edge4,Edge7,Edge10,Edge30,Edge31,Edge32,Edge33,Edge34,Edge35,Edge36,Edge37]
FEATURE [Part::Fillet] Fillet002  label="bumpperMain003"
  Base = -> Fillet001
  Edges = 11 edges r=1.2: [Edge4,Edge9,Edge13,Edge14,Edge15,Edge16,Edge17,Edge18,Edge19,Edge20,Edge21]
FEATURE [Part::Cylinder] Cylinder004  label="brace"
  Angle = 360
  AttacherType = Attacher::AttachEngine3D
  FirstAngle = 0
  Height = 32
  Placement = pos=(-42,0,0) rot=(0,1,0;1.5708rad)
  Radius = 2
  SecondAngle = 0
FEATURE [Part::Cylinder] Cylinder005  label="brace001"
  Angle = 360
  AttacherType = Attacher::AttachEngine3D
  FirstAngle = 0
  Height = 10
  Placement = pos=(29,0,0) rot=(0,1,0;1.5708rad)
  Radius = 2
  SecondAngle = 0
FEATURE [Part::Cylinder] Cylinder006  label="brace002"
  Angle = 360
  AttacherType = Attacher::AttachEngine3D
  FirstAngle = 0
  Height = 10
  Placement = pos=(-42,0,0) rot=(0,1,0;1.5708rad)
  Radius = 2
  SecondAngle = 0
FEATURE [Part::MultiFuse] Fusion008  label="leftBrace"
  Placement = pos=(-23,2,8) rot=(0,0,1;-0.785398rad)
  Shapes = -> [Cylinder004,Cylinder006]
FEATURE [Part::Cylinder] Cylinder007  label="brace003"
  Angle = 360
  AttacherType = Attacher::AttachEngine3D
  FirstAngle = 0
  Height = 32
  Placement = pos=(29,0,0) rot=(0,1,0;1.5708rad)
  Radius = 2
  SecondAngle = 0
FEATURE [Part::MultiFuse] Fusion009  label="rightBrace"
  Placement = pos=(6.4,-12,7) rot=(0,0,1;0.785398rad)
  Shapes = -> [Cylinder007,Cylinder005]
FEATURE [Part::Box] Box005  label="Cube"
  AttacherType = Attacher::AttachEngine3D
  Height = 40
  Length = 44
  Placement = pos=(41,47,-6) rot=(0,0,1;-0.349066rad)
  Width = 20
FEATURE [Part::Box] Box006  label="Cube001"
  AttacherType = Attacher::AttachEngine3D
  Height = 40
  Length = 44
  Placement = pos=(-85.35,31.95,-6) rot=(0,0,1;0.349066rad)
  Width = 20
